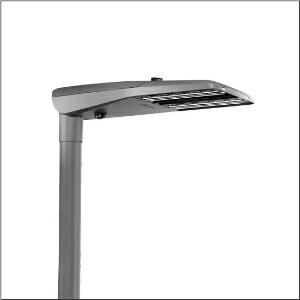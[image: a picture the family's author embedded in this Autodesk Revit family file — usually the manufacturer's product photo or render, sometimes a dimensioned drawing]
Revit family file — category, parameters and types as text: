
# Revit family: streetlight_sl_11_iq_midi___pc-l_5xc3e21y08me_ec69
name_source: partatom
category: Lighting Fixtures
units: mm (PartAtom-declared; Revit-internal decimal feet)

## family parameters
Cut with Voids When Loaded = No
Host = Face
Light Source = No
Part Type = Normal
Room Calculation Point = No
Round Connector Dimension = Use Diameter
Shared = No

## types (1)
- --- (1 x LED, 12730 lm, 122.8 W, 2200K)
    Apparent Load = 123 VA
    CIE Flux Codes = 37 73 96 100 100
    Color Rendering = 70
    Color Temperature = 2200K
    Default Elevation = 1800 mm
    Description = Streetlight SL 11 iQ midi, mast luminaire, primary light control with 3 zone facetted reflector, of plastic, silver coated, highly specular, primary optical cover: cover, of PMMA, transparent, light distribution: PC-L, light emission: direct distribution, primary light characteristic: asymmetric, left, installation type: post-top, side-entry, LED, High Power LED, rated luminous flux: 12.730lm, luminous efficacy: 104lm/W, light colour: 722, colour temperature: 2200K, control gear: iQ-Street Remote, D4i with power reduction, control: pre-setting: logarithmic dimming characteristic, Street-Remote, Auto-Match, Temp-Guard, Lumen-Switch, Night-Set, Smart-Wire, Light-Fading, Desk-Remote (wireless, voltage-free reading and setting of iQ features in the workshop via application-optimized NFC function/RFID function), optimised constant luminous flux control (CLO 2.0), with cable H07RN-F 5x 1.5mm², mains connection: 230..240V, AC, 50/60Hz, connection cable pre-assembled, cable length: 12,5m, start of lifetime: 123W, end of service life: 130W, reduction: 56W, luminaire housing, of diecast aluminium, powder-coated, Siteco® metallic grey (DB 702S), please order mast flange separately, inclination adjustable without tools: 0°, 5°, 10°, 15° (post-top) | 0°, -5°, -10°, -15° (side-entry), sealing non-destructively replaceable, multi-level sealing system, length: 780mm, width: 376mm, height: 118mm, mast flange for spigot size: 42mm (side-entry): 5XC10008XM4, 60/48mm (side-entry/post-top): 5XC10108XM2, 76/60mm (side-entry/post-top): 5XC10108XM1, mounting height: 6..12m, equipment: Power, Smart Interface below and above, protection rating (complete): IP66, insulation class (complete): insulation class II (safety insulation), certification: CE, ENEC, VDE, UKCA, impact resistance: IK09, permissible operating ambient temperature for outdoor applications: -25..+50°C, standard-compliant lighting for roads and squares, Environmental Product Declaration (EPD) tested and certified by an independent institute, packaging unit: 1 piece

Light Distribution: PC-L
    Height = 118 mm
    Lamp = 1 x LED
    Lamp Light Flux = 12730 lm
    Lamp Power = 122.8 W
    Lamp count = 1
    Length = 780 mm
    Luminous efficacy = 104 lm/W
    Manufacturer = Siteco
    ModVariant = No
    Model = 5XC3E21Y08ME
    Number of Poles = 1
    OnlyDefault = Yes
    Power Factor = 1
    Product Name = Streetlight SL 11 iQ midi | PC-L
    Product group = mast luminaire | pylon top
    ProductGroupID = 6100
    Protection Class = Protection class II
    Protection Degree = IP 66
    RLX_Detail_Level = 1
    RLX_Emergency_Light_Flux = 0 lm
    RLX_Emergency_Type = 0
    RLX_Emergency_Type_DB = No
    RlxData = <blob elided: 73593 chars, md5=977dc548>
    Socket = socket
    Standby Power = 0 W
    System Light Flux = 12729 lm
    System Power = 123 W
    Type Comments = factory setting: luminous flux: 100 % | dim-lin: 254 | 553 mA
    Type Image = l_1004429.jpg
    URL = http://relux.com
    VarID = @adj_121958
    Voltage = 0 V
    Weight = 0.00 kg
    Width = 376 mm

## geometry (parser evidence)
native form markers: Blend x4, Sweep x10
no freeform markers — native parametric forms only
